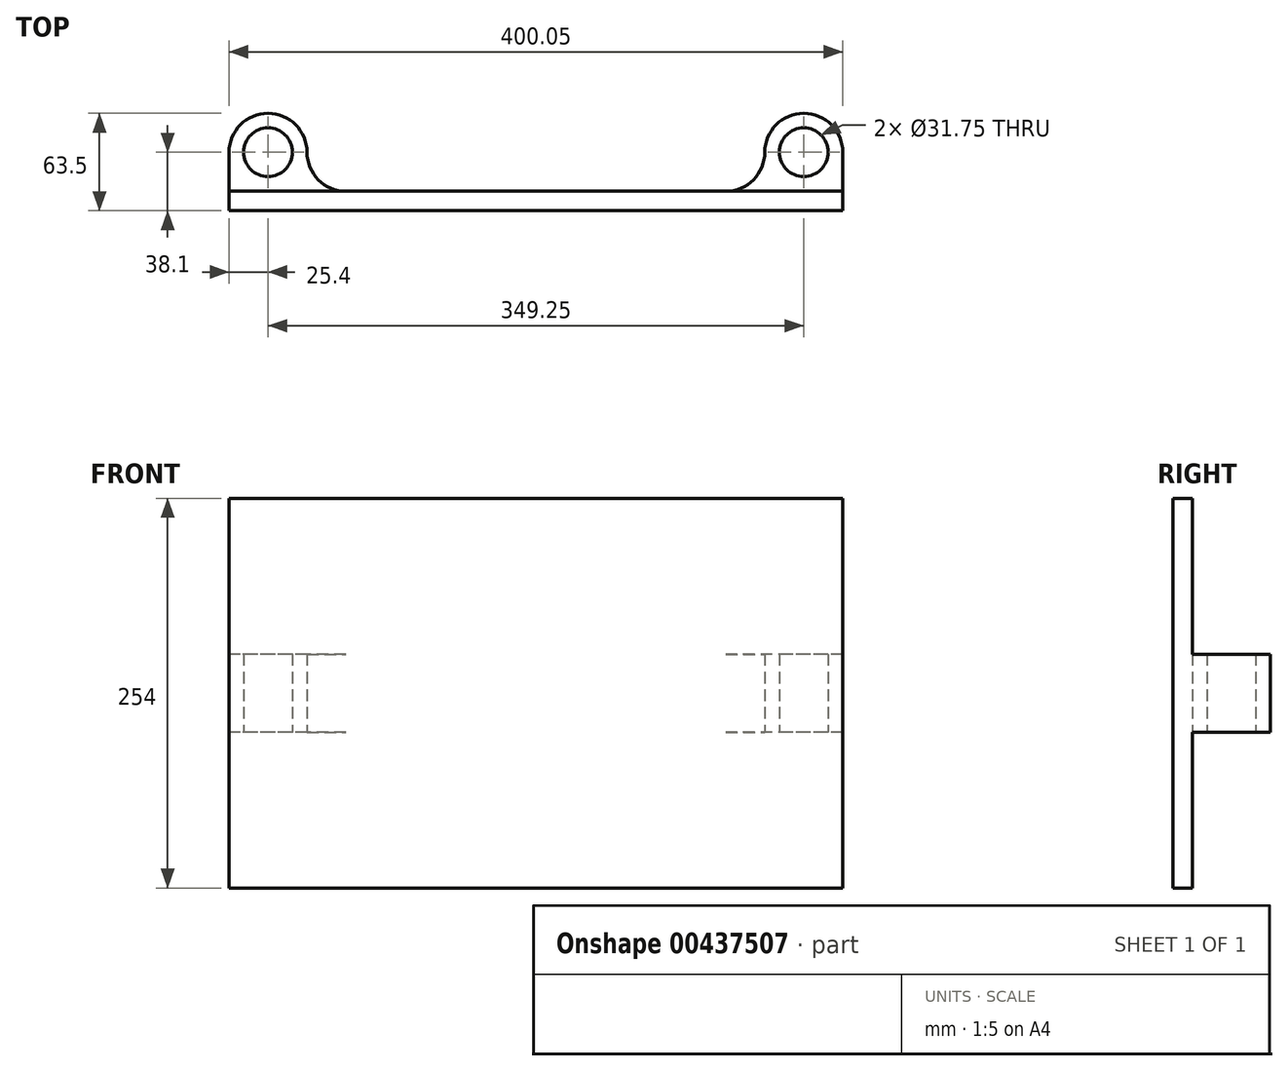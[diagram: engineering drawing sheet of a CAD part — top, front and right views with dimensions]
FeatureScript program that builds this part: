
annotation { "Feature Type Name" : "Feature", "Feature Type Description" : "" }
export const myFeature = defineFeature(function(context is Context, id is Id, definition is map)
    precondition{}
    {
        {
            var Q0;
            Q0=qCreatedBy(makeId("Front.planeOp"),FACE);
            var sketch = newSketch(context, id + "F0", { "sketchPlane" : qUnion([Q0])});
            skLineSegment(sketch, "E0.bottom", {"start": v(0, 0) * mm, "end": v(457.2, 0) * mm});
            skLineSegment(sketch, "E0.top", {"start": v(0, -254) * mm, "end": v(457.2, -254) * mm});
            skLineSegment(sketch, "E0.left", {"start": v(0, 0) * mm, "end": v(0, -254) * mm});
            skLineSegment(sketch, "E0.right", {"start": v(457.2, 0) * mm, "end": v(457.2, -254) * mm});
            skSolve(sketch);
        }
        {
            var Q0;
            Q0 = qSketchRegion(id + "F0", true);
            extrude(context, id + "F1", {"entities" : qUnion([Q0]), "depth" : 12.7 * mm, "offsetDistance" : 25.4 * mm});
        }
        {
            var Q0;
            Q0=qCreatedBy(makeId("Top.planeOp"),FACE);
            cPlane(context, id + "F2", {"entities" : qUnion([Q0]), "cplaneType" : CPlaneType.OFFSET, "offset" : 127 * mm, "oppositeDirection" : true, "width" : 152.4 * mm, "height" : 152.4 * mm});
        }
        {
            var Q0;
            Q0=qCreatedBy(id+"F2.planeOp",FACE);
            var sketch = newSketch(context, id + "F3", { "sketchPlane" : qUnion([Q0])});
            skLineSegment(sketch, "E1", {"start": v(0, 0) * mm, "end": v(50.8, 0) * mm});
            skLineSegment(sketch, "E2.MirrorCS", {"start": v(76.2, 0) * mm, "end": v(50.8, 0) * mm});
            skCircle(sketch, "E3.MirrorC", {"center": v(50.8, 25.4) * mm, "radius": 15.88 * mm});
            skLineSegment(sketch, "E4.MirrorCS", {"start": v(25.4, 0) * mm, "end": v(0, 0) * mm});
            skArc(sketch, "E5.MirrorCS", {"start": v(25.4, 25.4) * mm, "mid": v(50.8, 50.8) * mm, "end": v(76.2, 25.4) * mm});
            skLineSegment(sketch, "E6.MirrorCS", {"start": v(76.2, 0) * mm, "end": v(101.6, 0) * mm});
            skLineSegment(sketch, "E7.MirrorCS", {"start": v(76.2, 0) * mm, "end": v(25.4, 0) * mm});
            skArc(sketch, "E8.MirrorCS", {"start": v(101.6, 0) * mm, "mid": v(83.64, 7.44) * mm, "end": v(76.2, 25.4) * mm});
            skArc(sketch, "E9.MirrorCS", {"start": v(0, 0) * mm, "mid": v(17.96, 7.44) * mm, "end": v(25.4, 25.4) * mm});
            skLineSegment(sketch, "E10", {"start": v(0, 0) * mm, "end": v(225.43, 0) * mm});
            skLineSegment(sketch, "E11.MirrorCS", {"start": v(450.85, 0) * mm, "end": v(400.05, 0) * mm});
            skLineSegment(sketch, "E12.MirrorCS", {"start": v(374.65, 0) * mm, "end": v(400.05, 0) * mm});
            skArc(sketch, "E13.MirrorCS", {"start": v(349.25, 0) * mm, "mid": v(367.21, 7.44) * mm, "end": v(374.65, 25.4) * mm});
            skArc(sketch, "E14.MirrorCS", {"start": v(425.45, 25.4) * mm, "mid": v(400.05, 50.8) * mm, "end": v(374.65, 25.4) * mm});
            skCircle(sketch, "E15.MirrorC", {"center": v(400.05, 25.4) * mm, "radius": 15.88 * mm});
            skLineSegment(sketch, "E16.MirrorCS", {"start": v(425.45, 0) * mm, "end": v(450.85, 0) * mm});
            skArc(sketch, "E17.MirrorCS", {"start": v(450.85, 0) * mm, "mid": v(432.89, 7.44) * mm, "end": v(425.45, 25.4) * mm});
            skLineSegment(sketch, "E18.MirrorCS", {"start": v(374.65, 0) * mm, "end": v(349.25, 0) * mm});
            skLineSegment(sketch, "E19.MirrorCS", {"start": v(374.65, 0) * mm, "end": v(425.45, 0) * mm});
            skSolve(sketch);
        }
        {
            var Q0;
            Q0 = qSketchRegion(id + "F3", true);
            extrude(context, id + "F4", {"entities" : qUnion([Q0]), "operationType" : NewBodyOperationType.ADD, "depth" : 25.4 * mm, "offsetDistance" : 25.4 * mm, "hasSecondDirection" : true, "secondDirectionOppositeDirection" : true, "secondDirectionDepth" : 25.4 * mm});
        }
        {
            var Q0;
            Q0=qCreatedBy(id+"F2.planeOp",FACE);
            var sketch = newSketch(context, id + "F5", { "sketchPlane" : qUnion([Q0])});
            skLineSegment(sketch, "E20", {"start": v(0, 0) * mm, "end": v(25.4, 0) * mm});
            skLineSegment(sketch, "E21", {"start": v(25.4, 0) * mm, "end": v(25.4, 52.37) * mm});
            skLineSegment(sketch, "E22", {"start": v(25.4, 52.37) * mm, "end": v(-28.9, 52.37) * mm});
            skLineSegment(sketch, "E23", {"start": v(-28.9, 52.37) * mm, "end": v(-28.9, -43.34) * mm});
            skLineSegment(sketch, "E24", {"start": v(-28.9, -43.34) * mm, "end": v(25.4, -43.34) * mm});
            skLineSegment(sketch, "E25", {"start": v(25.4, -43.34) * mm, "end": v(25.4, 0) * mm});
            skLineSegment(sketch, "E26", {"start": v(0, 0) * mm, "end": v(225.43, 0) * mm});
            skLineSegment(sketch, "E27.MirrorCS", {"start": v(450.85, 0) * mm, "end": v(425.45, 0) * mm});
            skLineSegment(sketch, "E28.MirrorCS", {"start": v(425.45, 0) * mm, "end": v(425.45, 52.37) * mm});
            skLineSegment(sketch, "E29.MirrorCS", {"start": v(425.45, -43.34) * mm, "end": v(425.45, 0) * mm});
            skLineSegment(sketch, "E30.MirrorCS", {"start": v(479.75, 52.37) * mm, "end": v(479.75, -43.34) * mm});
            skLineSegment(sketch, "E31.MirrorCS", {"start": v(479.75, -43.34) * mm, "end": v(425.45, -43.34) * mm});
            skLineSegment(sketch, "E32.MirrorCS", {"start": v(425.45, 52.37) * mm, "end": v(479.75, 52.37) * mm});
            skSolve(sketch);
        }
        {
            var Q0;
            Q0 = qSketchRegion(id + "F5", true);
            var Q1;
            Q1=makeQuery(id+"F1.opExtrude","SWEPT_FACE",FACE,{"disambiguationData":[OSD([sQuery(id+"F0.wireOp",EDGE,"E0.top")])]});
            var Q2;
            Q2=makeQuery(id+"F1.opExtrude","SWEPT_FACE",FACE,{"disambiguationData":[OSD([sQuery(id+"F0.wireOp",EDGE,"E0.bottom")])]});
            extrude(context, id + "F6", {"entities" : qUnion([Q0]), "operationType" : NewBodyOperationType.REMOVE, "endBound" : BoundingType.UP_TO_SURFACE, "oppositeDirection" : true, "depth" : 137.16 * mm, "endBoundEntityFace" : qUnion([Q1]), "offsetDistance" : 25.4 * mm, "hasSecondDirection" : true, "secondDirectionBound" : SecondDirectionBoundingType.UP_TO_SURFACE, "secondDirectionOppositeDirection" : false, "secondDirectionDepth" : 106.68 * mm, "secondDirectionBoundEntityFace" : qUnion([Q2])});
        }
    });
